# Revit family: Bidet_Seat-DXV-Spalet-AT100
name_source: partatom
category: Specialty Equipment
units: mm (PartAtom-declared; Revit-internal decimal feet)

## family parameters
Always vertical = No
Cut with Voids When Loaded = No
OmniClass Number = 23.45.05.14.27
OmniClass Title = Bidets
Part Type = Normal
Room Calculation Point = No
Round Connector Dimension = Use Radius
Shared = Yes
Work Plane-Based = Yes

## types (1)
- AT100
    Assembly Code = D2010910
    Bowl Shape = Elongated
    Compliance Certifications = Meets or Exceeds the Following Specifications: • ASME A112.4.2/CSA B45.16 • Personal Hygiene and Health Care Appliances - UL 1431 • Motor-operated appliances (household and commercial) -
CSA C22.2 No. 68-14 • Update No. 3 • Household Cooking and Liquid-Heating Appliances - CSA C22.2 No. 64-14 • UPC• IPC• NSPC• NPC Canada
    Default Elevation = 0"
    Description = AT100® Electric Elongated SpaLet® Bidet Seat
    Finish = Plastic-DXV-415-Canvas White
    Height = 6 3/8"
    Installation Type = Toilet Mounted
    Length = 21 1/2"
    Manufacturer = DXV
    Material = Plastic-DXV-415-Canvas White
    Model = AT100-(D28005ARS141-415)
    Product Documentation Link = https://americanstandard.box.com
    Product Page URL = https://www.dxv.com
    Revised Date = 05/17/2023
    URL = http://www.dxv.com
    Warranty Information = Limited Lifetime Warranty
    Width = 16 3/4"
    cUPC Compliant = Yes

## geometry (parser evidence)
native form markers: Sweep x2
no freeform markers — native parametric forms only
